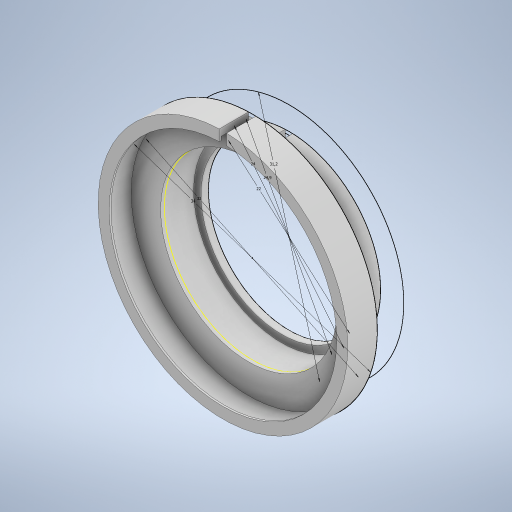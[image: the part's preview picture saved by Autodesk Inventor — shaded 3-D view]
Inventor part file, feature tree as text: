
AUTODESK INVENTOR PART (.ipt)
format: ipt  version: 2023 (Build 270158000, 158)  size: 340,992 bytes
history: native  units: mm
features: extrude x7, sketch x5
ambient origin geometry x8: Origin, YZ Plane, XZ Plane, XY Plane, X Axis, Y Axis, Z Axis, Center Point
bodies: Solid1 (feature_tree)
feature tree (12):
  sketch  "Sketch1"  dims[d0=24.9mm d1=22.0mm]
  extrude  "Extrusion1"  Depth=22.0mm
  extrude  "Extrusion2"  Depth=24.0mm
  extrude  "Extrusion3"  Depth=4.0mm TaperAngle=0.0deg
  sketch  "Sketch4"  dims[d4=1.0mm d5=0.0mm d6=4.0mm d7=0.0mm]
  extrude  "Extrusion5"  Depth=1.0mm
  extrude  "Extrusion6"  Depth=0.5mm TaperAngle=0.0deg
  extrude  "Extrusion7"  Depth=4.0mm TaperAngle=0.0deg
  extrude  "Extrusion10"  Depth=10.0mm
  sketch  "Sketch2"  dims[d2=31.2mm d3=24.0mm]
  sketch  "Sketch5"  dims[d8=1.0mm d9=0.0mm d14=32.0mm]
  sketch  "Sketch8"  dims[d15=34.0mm d16=0.5mm d17=0.0mm d18=4.0mm d19=0.0mm d20=31.0mm d21=0.25mm d22=0.0mm d30=1.0mm d31=10.0mm d32=10.0mm d33=0.0mm]
